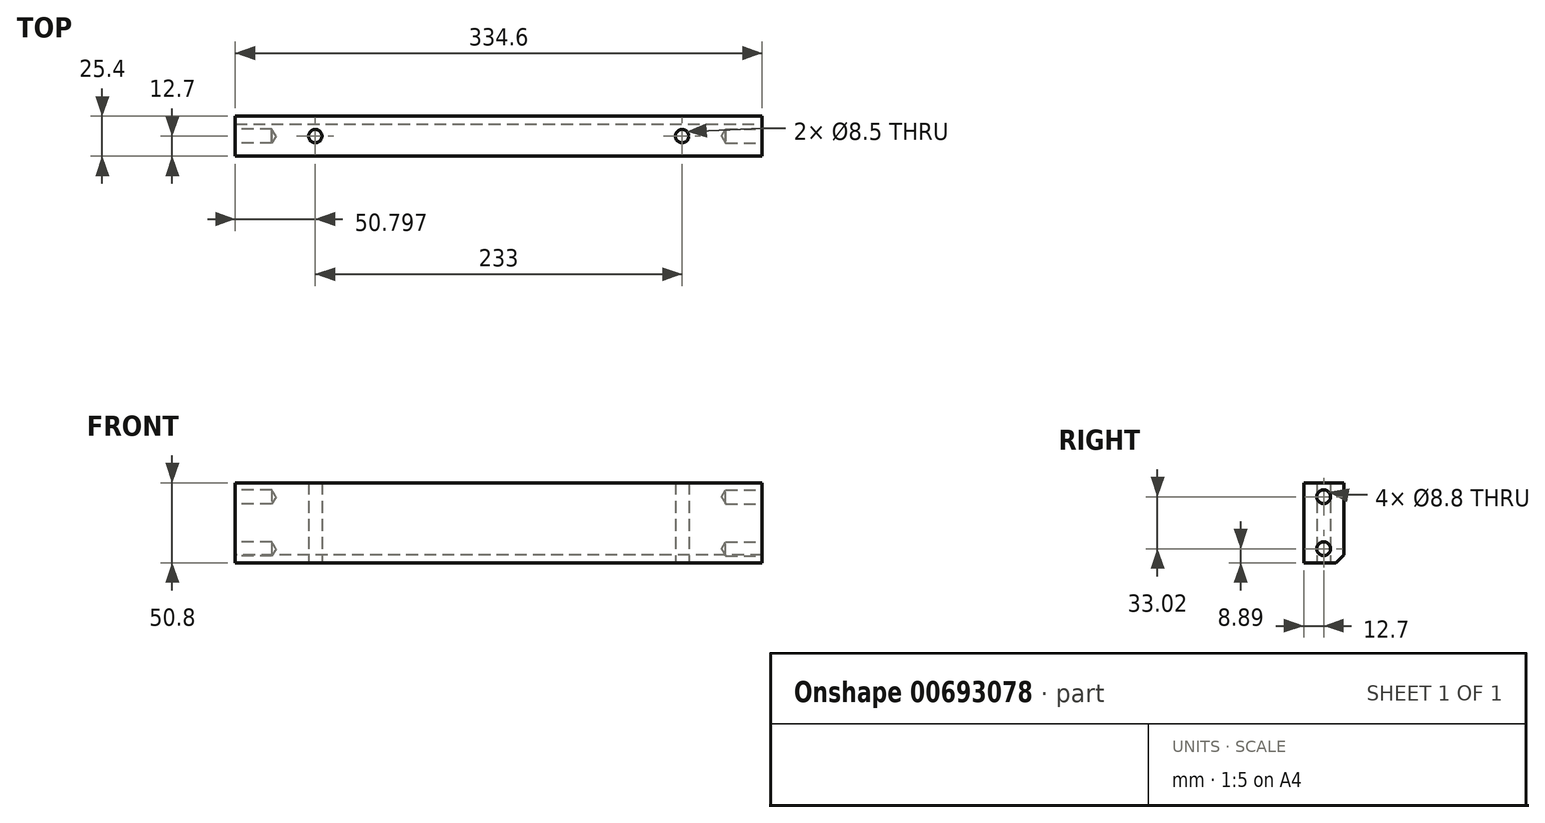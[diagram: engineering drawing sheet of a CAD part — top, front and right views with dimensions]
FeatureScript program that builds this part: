
annotation { "Feature Type Name" : "Feature", "Feature Type Description" : "" }
export const myFeature = defineFeature(function(context is Context, id is Id, definition is map)
    precondition{}
    {
        {
            var Q0;
            Q0=qCreatedBy(makeId("Top.planeOp"),FACE);
            var sketch = newSketch(context, id + "F0", { "sketchPlane" : qUnion([Q0])});
            skLineSegment(sketch, "E0.bottom", {"start": v(-2.71, 0) * mm, "end": v(331.89, 0) * mm});
            skLineSegment(sketch, "E0.top", {"start": v(-2.71, 25.4) * mm, "end": v(331.89, 25.4) * mm});
            skLineSegment(sketch, "E0.left", {"start": v(-2.71, 0) * mm, "end": v(-2.71, 25.4) * mm});
            skLineSegment(sketch, "E0.right", {"start": v(331.89, 0) * mm, "end": v(331.89, 25.4) * mm});
            skSolve(sketch);
        }
        {
            var Q0;
            Q0=makeQuery(id+"F0.imprint","IMPRINT",FACE,{"disambiguationData":[TD([[makeQuery(id+"F0.imprint","IMPRINT",EDGE,{"derivedFrom":sQuery(id+"F0.wireOp",EDGE,"E0.bottom")}),1.0]])]});
            extrude(context, id + "F1", {"entities" : qUnion([Q0]), "depth" : 50.8 * mm, "offsetDistance" : 25.4 * mm});
        }
        {
            var Q0;
            Q0=makeQuery(id+"F1.opExtrude","SWEPT_FACE",FACE,{"disambiguationData":[OSD([sQuery(id+"F0.wireOp",EDGE,"E0.right")])]});
            var sketch = newSketch(context, id + "F2", { "sketchPlane" : qUnion([Q0])});
            skLineSegment(sketch, "E1", {"start": v(12.7, 50.8) * mm, "end": v(12.7, 41.91) * mm});
            skLineSegment(sketch, "E2", {"start": v(12.7, 0) * mm, "end": v(12.7, 8.9) * mm});
            skSolve(sketch);
        }
        {
            var Q0;
            Q0=makeQuery(id+"F1.opExtrude","SWEPT_FACE",FACE,{"disambiguationData":[OSD([sQuery(id+"F0.wireOp",EDGE,"E0.left")])]});
            var sketch = newSketch(context, id + "F3", { "sketchPlane" : qUnion([Q0])});
            skLineSegment(sketch, "E3.0", {"start": v(-12.7, 50.8) * mm, "end": v(-12.7, 41.91) * mm});
            skLineSegment(sketch, "E4.0", {"start": v(-12.7, 0) * mm, "end": v(-12.7, 8.9) * mm});
            skSolve(sketch);
        }
        {
            var Q0;
            Q0=sQuery(id+"F3.wireOp",VERTEX,"E3.0.end");
            var Q1;
            Q1=sQuery(id+"F3.wireOp",VERTEX,"E4.0.end");
            var Q2;
            Q2=sQuery(id+"F2.wireOp",VERTEX,"E1.end");
            var Q3;
            Q3=sQuery(id+"F2.wireOp",VERTEX,"E2.end");
            var Q4;
            Q4=makeQuery(id+"F1.opExtrude","SWEPT_BODY",BODY,{"disambiguationData":[OSD([sQuery(id+"F0.wireOp",EDGE,"E0.bottom"),sQuery(id+"F0.wireOp",EDGE,"E0.top"),sQuery(id+"F0.wireOp",EDGE,"E0.left"),sQuery(id+"F0.wireOp",EDGE,"E0.right")])]});
            hole(context, id + "F4", {"style" : HoleStyle.SIMPLE, "endStyle" : HoleEndStyle.BLIND, "standardTappedOrClearance" : lookupTablePath({ "standard" : "ISO", "engagement" : "75%", "pitch" : "1.25 mm", "size" : "M10", "type" : "Tapped" }), "standardBlindInLast" : lookupTablePath({ "standard" : "ISO", "engagement" : "75%", "pitch" : "1.25 mm", "size" : "M10", "type" : "Tapped" }), "holeDiameter" : 8.8 * mm, "majorDiameter" : 10 * mm, "showTappedDepth" : true, "holeDepth" : 23.13 * mm, "tappedDepth" : 19.38 * mm, "tapClearance" : 3, "locations" : qUnion([Q0, Q1, Q2, Q3]), "scope" : qUnion([Q4])});
        }
        {
            var Q0;
            Q0=makeQuery(id+"F1.opExtrude","CAP_EDGE",EDGE,{"disambiguationData":[OSD([sQuery(id+"F0.wireOp",EDGE,"E0.top")])],"isStart":true});
            chamfer(context, id + "F5", {"entities" : qUnion([Q0]), "width" : 5.08 * mm, "tangentPropagation" : true});
        }
        {
            var Q0;
            Q0=makeQuery(id+"F1.opExtrude","CAP_FACE",FACE,{"disambiguationData":[OSD([sQuery(id+"F0.wireOp",EDGE,"E0.bottom"),sQuery(id+"F0.wireOp",EDGE,"E0.top"),sQuery(id+"F0.wireOp",EDGE,"E0.left"),sQuery(id+"F0.wireOp",EDGE,"E0.right")])],"isStart":true});
            var sketch = newSketch(context, id + "F6", { "sketchPlane" : qUnion([Q0])});
            skLineSegment(sketch, "E5", {"start": v(-2.71, 0) * mm, "end": v(-2.71, -12.7) * mm});
            skLineSegment(sketch, "E6", {"start": v(-2.71, -12.7) * mm, "end": v(48.09, -12.7) * mm});
            skLineSegment(sketch, "E7", {"start": v(331.89, 0) * mm, "end": v(331.89, -12.7) * mm});
            skLineSegment(sketch, "E8", {"start": v(331.89, -12.7) * mm, "end": v(281.09, -12.7) * mm});
            skSolve(sketch);
        }
        {
            var Q0;
            Q0=sQuery(id+"F6.wireOp",VERTEX,"RAnJ8e52-AIoe-Ubsq-hwi4-Y3Cf9GMspgCn.end");
            var Q1;
            Q1=sQuery(id+"F6.wireOp",VERTEX,"ImLu8xNf-lyD7-Dvmo-gDWg-cQjJC2BbcEMu.end");
            var Q2;
            Q2=sQuery(id+"F6.wireOp",VERTEX,"E6.end");
            var Q3;
            Q3=sQuery(id+"F6.wireOp",VERTEX,"E8.end");
            var Q4;
            Q4=makeQuery(id+"F1.opExtrude","SWEPT_BODY",BODY,{"disambiguationData":[OSD([sQuery(id+"F0.wireOp",EDGE,"E0.bottom"),sQuery(id+"F0.wireOp",EDGE,"E0.top"),sQuery(id+"F0.wireOp",EDGE,"E0.left"),sQuery(id+"F0.wireOp",EDGE,"E0.right")])]});
            hole(context, id + "F7", {"style" : HoleStyle.SIMPLE, "endStyle" : HoleEndStyle.THROUGH, "standardTappedOrClearance" : lookupTablePath({ "standard" : "ISO", "engagement" : "75%", "pitch" : "1.5 mm", "size" : "M10", "type" : "Tapped" }), "standardBlindInLast" : lookupTablePath({ "standard" : "ISO", "engagement" : "75%", "pitch" : "1.5 mm", "size" : "M10", "type" : "Tapped" }), "holeDiameter" : 8.5 * mm, "majorDiameter" : 10 * mm, "showTappedDepth" : true, "tappedDepth" : 19.38 * mm, "tapClearance" : 3, "locations" : qUnion([Q0, Q1, Q2, Q3]), "scope" : qUnion([Q4])});
        }
    });
